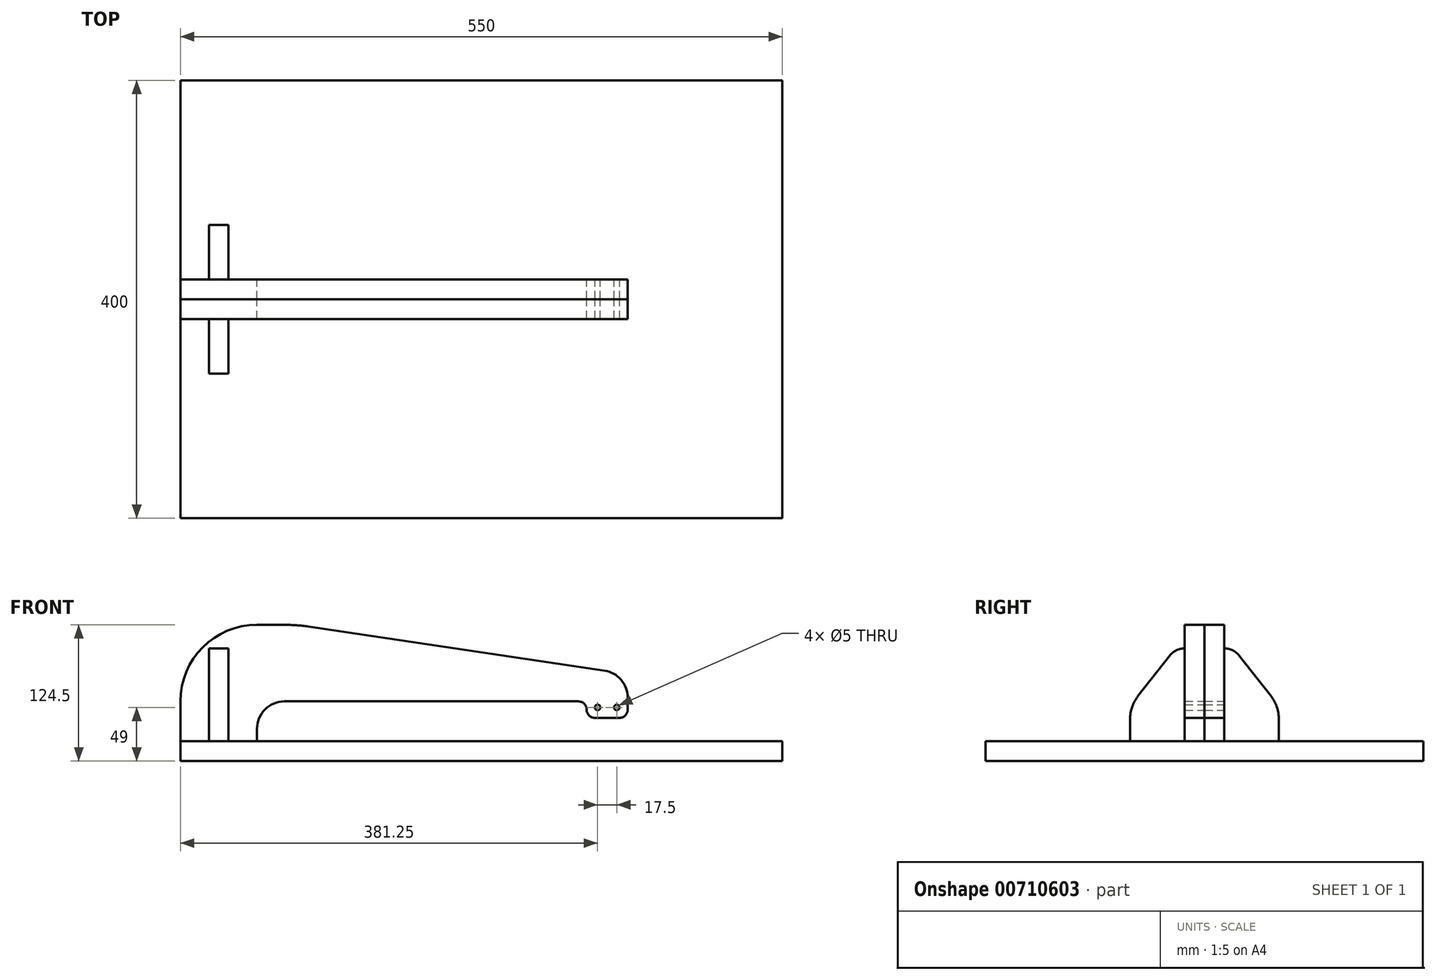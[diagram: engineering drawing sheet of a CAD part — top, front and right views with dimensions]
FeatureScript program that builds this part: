
annotation { "Feature Type Name" : "Feature", "Feature Type Description" : "" }
export const myFeature = defineFeature(function(context is Context, id is Id, definition is map)
    precondition{}
    {
        {
            var Q0;
            Q0=qCreatedBy(makeId("Front.planeOp"),FACE);
            var sketch = newSketch(context, id + "F0", { "sketchPlane" : qUnion([Q0])});
            skLineSegment(sketch, "E0", {"start": v(0, 0) * mm, "end": v(70, 0) * mm});
            skLineSegment(sketch, "E1", {"start": v(70, 0) * mm, "end": v(70, 11.5) * mm});
            skLineSegment(sketch, "E2", {"start": v(95, 36.5) * mm, "end": v(363.75, 36.5) * mm});
            skLineSegment(sketch, "E3", {"start": v(371.25, 29) * mm, "end": v(371.25, 29) * mm});
            skLineSegment(sketch, "E4", {"start": v(378.75, 21.5) * mm, "end": v(401.25, 21.5) * mm});
            skLineSegment(sketch, "E5", {"start": v(408.75, 29) * mm, "end": v(408.75, 39.94) * mm});
            skLineSegment(sketch, "E6", {"start": v(387.43, 64.67) * mm, "end": v(117.06, 104.87) * mm});
            skLineSegment(sketch, "E7", {"start": v(95, 106.5) * mm, "end": v(70, 106.5) * mm});
            skLineSegment(sketch, "E8", {"start": v(0, 36.5) * mm, "end": v(0, 0) * mm});
            skPoint(sketch, "E9", {"position": v(390, 21.5) * mm});
            skCircle(sketch, "E10", {"center": v(381.25, 31) * mm, "radius": 8 * mm, "construction": true});
            skCircle(sketch, "E11", {"center": v(398.75, 31) * mm, "radius": 8 * mm, "construction": true});
            skLineSegment(sketch, "E12", {"start": v(381.25, 31) * mm, "end": v(398.75, 31) * mm, "construction": true});
            skPoint(sketch, "E13.endSnap0", {"position": v(390, 31) * mm});
            skLineSegment(sketch, "E14", {"start": v(390, 31) * mm, "end": v(390, 21.5) * mm, "construction": true});
            skCircle(sketch, "E15", {"center": v(381.25, 31) * mm, "radius": 2.5 * mm});
            skCircle(sketch, "E16", {"center": v(398.75, 31) * mm, "radius": 2.5 * mm});
            skLineSegment(sketch, "E17.bottom", {"start": v(0, 0) * mm, "end": v(408.75, 0) * mm, "construction": true});
            skLineSegment(sketch, "E17.top", {"start": v(0, -18) * mm, "end": v(408.75, -18) * mm, "construction": true});
            skLineSegment(sketch, "E17.left", {"start": v(0, 0) * mm, "end": v(0, -18) * mm, "construction": true});
            skLineSegment(sketch, "E17.right", {"start": v(408.75, 0) * mm, "end": v(408.75, -18) * mm, "construction": true});
            skPoint(sketch, "E18.visualSharp", {"position": v(0, 106.5) * mm});
            skArc(sketch, "E18.filletArc", {"start": v(70, 106.5) * mm, "mid": v(20.5, 86) * mm, "end": v(0, 36.5) * mm});
            skArc(sketch, "E19.filletArc", {"start": v(95, 36.5) * mm, "mid": v(77.32, 29.18) * mm, "end": v(70, 11.5) * mm});
            skPoint(sketch, "E20.visualSharp", {"position": v(408.75, 61.5) * mm});
            skArc(sketch, "E20.filletArc", {"start": v(408.75, 39.94) * mm, "mid": v(402.68, 56.27) * mm, "end": v(387.43, 64.67) * mm});
            skPoint(sketch, "E21.visualSharp", {"position": v(371.25, 36.5) * mm});
            skArc(sketch, "E21.filletArc", {"start": v(371.25, 29) * mm, "mid": v(369.05, 34.3) * mm, "end": v(363.75, 36.5) * mm});
            skPoint(sketch, "E22.visualSharp", {"position": v(371.25, 21.5) * mm});
            skArc(sketch, "E22.filletArc", {"start": v(371.25, 29) * mm, "mid": v(373.45, 23.7) * mm, "end": v(378.75, 21.5) * mm});
            skPoint(sketch, "E23.visualSharp", {"position": v(408.75, 21.5) * mm});
            skArc(sketch, "E23.filletArc", {"start": v(401.25, 21.5) * mm, "mid": v(406.55, 23.7) * mm, "end": v(408.75, 29) * mm});
            skPoint(sketch, "E24.visualSharp", {"position": v(106.1, 106.5) * mm});
            skArc(sketch, "E24.filletArc", {"start": v(117.06, 104.87) * mm, "mid": v(106.06, 106.1) * mm, "end": v(95, 106.5) * mm});
            skLineSegment(sketch, "E25", {"start": v(95, 106.5) * mm, "end": v(95, 36.5) * mm, "construction": true});
            skSolve(sketch);
        }
        {
            var Q0;
            Q0 = qSketchRegion(id + "F0", true);
            extrude(context, id + "F1", {"entities" : qUnion([Q0]), "depth" : 18 * mm, "offsetDistance" : 25 * mm});
        }
        {
            var Q0;
            Q0=makeQuery(id+"F1.opExtrude","SWEPT_BODY",BODY,{"disambiguationData":[OSD([sQuery(id+"F0.wireOp",EDGE,"E0"),sQuery(id+"F0.wireOp",EDGE,"E1"),sQuery(id+"F0.wireOp",EDGE,"E2"),sQuery(id+"F0.wireOp",EDGE,"E4"),sQuery(id+"F0.wireOp",EDGE,"E5"),sQuery(id+"F0.wireOp",EDGE,"E6"),sQuery(id+"F0.wireOp",EDGE,"E7"),sQuery(id+"F0.wireOp",EDGE,"E8"),sQuery(id+"F0.wireOp",EDGE,"E15"),sQuery(id+"F0.wireOp",EDGE,"E16"),sQuery(id+"F0.wireOp",EDGE,"E18.filletArc"),sQuery(id+"F0.wireOp",EDGE,"E19.filletArc"),sQuery(id+"F0.wireOp",EDGE,"E20.filletArc"),sQuery(id+"F0.wireOp",EDGE,"E21.filletArc"),sQuery(id+"F0.wireOp",EDGE,"E22.filletArc"),sQuery(id+"F0.wireOp",EDGE,"E23.filletArc"),sQuery(id+"F0.wireOp",EDGE,"E24.filletArc")])]});
            transform(context, id + "F2", {"entities" : qUnion([Q0]), "transformType" : TransformType.TRANSLATION_3D, "dx" : 0 * mm, "dy" : 18 * mm, "dz" : 0 * mm, "makeCopy" : true});
        }
        {
            var Q0;
            Q0=makeQuery(id+"F1.opExtrude","SWEPT_FACE",FACE,{"disambiguationData":[OSD([sQuery(id+"F0.wireOp",EDGE,"E0")])]});
            var sketch = newSketch(context, id + "F3", { "sketchPlane" : qUnion([Q0])});
            skLineSegment(sketch, "E26.bottom", {"start": v(0, -200) * mm, "end": v(550, -200) * mm});
            skLineSegment(sketch, "E26.top", {"start": v(0, 200) * mm, "end": v(550, 200) * mm});
            skLineSegment(sketch, "E26.left", {"start": v(0, -200) * mm, "end": v(0, 200) * mm});
            skLineSegment(sketch, "E26.right", {"start": v(550, -200) * mm, "end": v(550, 200) * mm});
            skSolve(sketch);
        }
        {
            var Q0;
            Q0 = qSketchRegion(id + "F3", true);
            extrude(context, id + "F4", {"entities" : qUnion([Q0]), "depth" : 18 * mm, "offsetDistance" : 25 * mm});
        }
        {
            var Q0;
            Q0=makeQuery(id+"F2.opPattern","COPY",FACE,{"derivedFrom":makeQuery(id+"F1.opExtrude","SWEPT_FACE",FACE,{"disambiguationData":[OSD([sQuery(id+"F0.wireOp",EDGE,"E8")])]}),"instanceName":"1"});
            var sketch = newSketch(context, id + "F5", { "sketchPlane" : qUnion([Q0])});
            skLineSegment(sketch, "E27", {"start": v(-18, 0) * mm, "end": v(-68, 0) * mm});
            skLineSegment(sketch, "E28", {"start": v(-18, 85) * mm, "end": v(-18, 0) * mm});
            skLineSegment(sketch, "E29", {"start": v(0, 0) * mm, "end": v(0, 123.16) * mm, "construction": true});
            skArc(sketch, "E30", {"start": v(-18, 85) * mm, "mid": v(-25.66, 83.24) * mm, "end": v(-31.77, 78.3) * mm});
            skLineSegment(sketch, "E31", {"start": v(-60.55, 41.6) * mm, "end": v(-31.77, 78.3) * mm});
            skLineSegment(sketch, "E32", {"start": v(-68, 0) * mm, "end": v(-68, 20) * mm});
            skPoint(sketch, "E33.visualSharp", {"position": v(-68, 32.08) * mm});
            skArc(sketch, "E33.filletArc", {"start": v(-60.55, 41.6) * mm, "mid": v(-66.08, 31.42) * mm, "end": v(-68, 20) * mm});
            skLineSegment(sketch, "E34.MirrorCS", {"start": v(18, 0) * mm, "end": v(68, 0) * mm});
            skLineSegment(sketch, "E35.MirrorCS", {"start": v(60.55, 41.6) * mm, "end": v(31.77, 78.3) * mm});
            skLineSegment(sketch, "E36.MirrorCS", {"start": v(68, 0) * mm, "end": v(68, 20) * mm});
            skPoint(sketch, "E37.MirrorP", {"position": v(68, 32.08) * mm});
            skArc(sketch, "E38.MirrorCS", {"start": v(18, 85) * mm, "mid": v(25.66, 83.24) * mm, "end": v(31.77, 78.3) * mm});
            skArc(sketch, "E39.MirrorCS", {"start": v(60.55, 41.6) * mm, "mid": v(66.08, 31.42) * mm, "end": v(68, 20) * mm});
            skLineSegment(sketch, "E40.MirrorCS", {"start": v(18, 85) * mm, "end": v(18, 0) * mm});
            skSolve(sketch);
        }
        {
            var Q0;
            Q0 = qSketchRegion(id + "F5", true);
            extrude(context, id + "F6", {"entities" : qUnion([Q0]), "oppositeDirection" : true, "depth" : (35 + 9) * mm, "offsetDistance" : 25 * mm, "hasSecondDirection" : true, "secondDirectionOppositeDirection" : true, "secondDirectionDepth" : (35 - 9) * mm});
        }
    });
